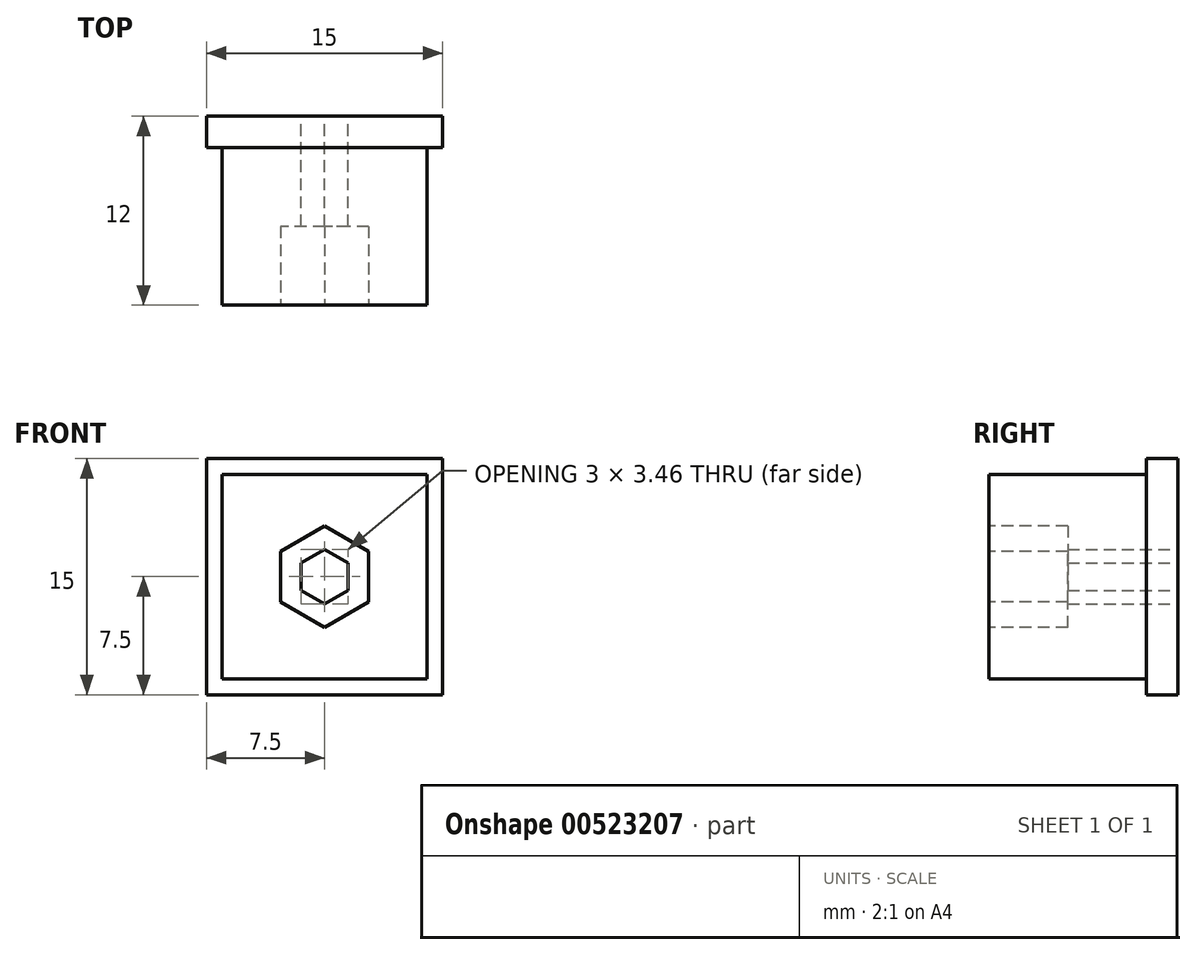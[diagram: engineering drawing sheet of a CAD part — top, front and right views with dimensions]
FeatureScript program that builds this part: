
annotation { "Feature Type Name" : "Feature", "Feature Type Description" : "" }
export const myFeature = defineFeature(function(context is Context, id is Id, definition is map)
    precondition{}
    {
        {
            var Q0;
            Q0=qCreatedBy(makeId("Front.planeOp"),FACE);
            var sketch = newSketch(context, id + "F0", { "sketchPlane" : qUnion([Q0])});
            skLineSegment(sketch, "E0.bottom", {"start": v(7.5, -7.5) * mm, "end": v(-7.5, -7.5) * mm});
            skLineSegment(sketch, "E0.top", {"start": v(7.5, 7.5) * mm, "end": v(-7.5, 7.5) * mm});
            skLineSegment(sketch, "E0.left", {"start": v(7.5, -7.5) * mm, "end": v(7.5, 7.5) * mm});
            skLineSegment(sketch, "E0.right", {"start": v(-7.5, -7.5) * mm, "end": v(-7.5, 7.5) * mm});
            skPoint(sketch, "E0.middle", {"position": v(0, 0) * mm});
            skSolve(sketch);
        }
        {
            var Q0;
            Q0=makeQuery(id+"F0.imprint","IMPRINT",FACE,{"disambiguationData":[TD([[makeQuery(id+"F0.imprint","IMPRINT",EDGE,{"derivedFrom":sQuery(id+"F0.wireOp",EDGE,"E0.bottom")}),-1.0]])]});
            extrude(context, id + "F1", {"entities" : qUnion([Q0]), "depth" : 2 * mm, "offsetDistance" : 25 * mm});
        }
        {
            var Q0;
            Q0=makeQuery(id+"F1.opExtrude","CAP_FACE",FACE,{"disambiguationData":[OSD([sQuery(id+"F0.wireOp",EDGE,"E0.bottom"),sQuery(id+"F0.wireOp",EDGE,"E0.top"),sQuery(id+"F0.wireOp",EDGE,"E0.left"),sQuery(id+"F0.wireOp",EDGE,"E0.right")])],"isStart":false});
            var sketch = newSketch(context, id + "F2", { "sketchPlane" : qUnion([Q0])});
            skLineSegment(sketch, "E1.0.0", {"start": v(7.5, -7.5) * mm, "end": v(7.5, 7.5) * mm});
            skLineSegment(sketch, "E1.0.1", {"start": v(7.5, 7.5) * mm, "end": v(-7.5, 7.5) * mm});
            skLineSegment(sketch, "E1.0.2", {"start": v(-7.5, 7.5) * mm, "end": v(-7.5, -7.5) * mm});
            skLineSegment(sketch, "E1.0.3", {"start": v(-7.5, -7.5) * mm, "end": v(7.5, -7.5) * mm});
            skLineSegment(sketch, "E2.0", {"start": v(6.5, -6.5) * mm, "end": v(6.5, 6.5) * mm});
            skLineSegment(sketch, "E2.1", {"start": v(-6.5, -6.5) * mm, "end": v(6.5, -6.5) * mm});
            skLineSegment(sketch, "E2.2", {"start": v(-6.5, 6.5) * mm, "end": v(-6.5, -6.5) * mm});
            skLineSegment(sketch, "E2.3", {"start": v(6.5, 6.5) * mm, "end": v(-6.5, 6.5) * mm});
            skSolve(sketch);
        }
        {
            var Q0;
            Q0=makeQuery(id+"F2.imprint","IMPRINT",FACE,{"disambiguationData":[TD([[makeQuery(id+"F2.imprint","IMPRINT",EDGE,{"derivedFrom":sQuery(id+"F2.wireOp",EDGE,"E2.0")}),1.0]])]});
            extrude(context, id + "F3", {"entities" : qUnion([Q0]), "operationType" : NewBodyOperationType.ADD, "depth" : 10 * mm, "offsetDistance" : 25 * mm});
        }
        {
            var Q0;
            Q0=makeQuery(id+"F1.opExtrude","CAP_FACE",FACE,{"disambiguationData":[OSD([sQuery(id+"F0.wireOp",EDGE,"E0.bottom"),sQuery(id+"F0.wireOp",EDGE,"E0.top"),sQuery(id+"F0.wireOp",EDGE,"E0.left"),sQuery(id+"F0.wireOp",EDGE,"E0.right")])],"isStart":true});
            var sketch = newSketch(context, id + "F4", { "sketchPlane" : qUnion([Q0])});
            skCircle(sketch, "E3.cCircle", {"center": v(0, 0) * mm, "radius": 1.5 * mm, "construction": true});
            skLineSegment(sketch, "E3.0", {"start": v(1.5, 0.87) * mm, "end": v(1.5, -0.87) * mm});
            skLineSegment(sketch, "E3.1", {"start": v(1.5, -0.87) * mm, "end": v(0, -1.73) * mm});
            skLineSegment(sketch, "E3.2", {"start": v(0, -1.73) * mm, "end": v(-1.5, -0.87) * mm});
            skLineSegment(sketch, "E3.3", {"start": v(-1.5, -0.87) * mm, "end": v(-1.5, 0.87) * mm});
            skLineSegment(sketch, "E3.4", {"start": v(-1.5, 0.87) * mm, "end": v(0, 1.73) * mm});
            skLineSegment(sketch, "E3.5", {"start": v(0, 1.73) * mm, "end": v(1.5, 0.87) * mm});
            skPoint(sketch, "E3.0.midPoint", {"position": v(1.5, 0) * mm});
            skSolve(sketch);
        }
        {
            var Q0;
            Q0=makeQuery(id+"F4.imprint","IMPRINT",FACE,{"disambiguationData":[TD([[makeQuery(id+"F4.imprint","IMPRINT",EDGE,{"derivedFrom":sQuery(id+"F4.wireOp",EDGE,"W7pu7vk7-25iV-fgy8-9aF9-MsBdlh5b4NGt")}),1.0]])]});
            var Q1;
            Q1=makeQuery(id+"F4.imprint","IMPRINT",FACE,{"disambiguationData":[TD([[makeQuery(id+"F4.imprint","IMPRINT",EDGE,{"derivedFrom":sQuery(id+"F4.wireOp",EDGE,"E3.0")}),-1.0]])]});
            extrude(context, id + "F5", {"entities" : qUnion([Q0, Q1]), "operationType" : NewBodyOperationType.REMOVE, "endBound" : BoundingType.UP_TO_NEXT, "oppositeDirection" : true, "depth" : 25 * mm, "offsetDistance" : 25 * mm});
        }
        {
            var Q0;
            Q0=makeQuery(id+"F3.opExtrude","CAP_FACE",FACE,{"disambiguationData":[OSD([sQuery(id+"F2.wireOp",EDGE,"E2.0"),sQuery(id+"F2.wireOp",EDGE,"E2.1"),sQuery(id+"F2.wireOp",EDGE,"E2.2"),sQuery(id+"F2.wireOp",EDGE,"E2.3")])],"isStart":false});
            var sketch = newSketch(context, id + "F6", { "sketchPlane" : qUnion([Q0])});
            skCircle(sketch, "E4.cCircle", {"center": v(0, 0) * mm, "radius": 2.8 * mm, "construction": true});
            skLineSegment(sketch, "E4.0", {"start": v(-2.8, -1.62) * mm, "end": v(-2.8, 1.62) * mm});
            skLineSegment(sketch, "E4.1", {"start": v(-2.8, 1.62) * mm, "end": v(0, 3.23) * mm});
            skLineSegment(sketch, "E4.2", {"start": v(0, 3.23) * mm, "end": v(2.8, 1.62) * mm});
            skLineSegment(sketch, "E4.3", {"start": v(2.8, 1.62) * mm, "end": v(2.8, -1.62) * mm});
            skLineSegment(sketch, "E4.4", {"start": v(2.8, -1.62) * mm, "end": v(0, -3.23) * mm});
            skLineSegment(sketch, "E4.5", {"start": v(0, -3.23) * mm, "end": v(-2.8, -1.62) * mm});
            skPoint(sketch, "E4.0.midPoint", {"position": v(-2.8, 0) * mm});
            skSolve(sketch);
        }
        {
            var Q0;
            Q0=makeQuery(id+"F6.imprint","IMPRINT",FACE,{"disambiguationData":[TD([[makeQuery(id+"F6.imprint","IMPRINT",EDGE,{"derivedFrom":sQuery(id+"F6.wireOp",EDGE,"E4.0")}),-1.0]])]});
            extrude(context, id + "F7", {"entities" : qUnion([Q0]), "operationType" : NewBodyOperationType.REMOVE, "oppositeDirection" : true, "depth" : 5 * mm, "offsetDistance" : 25 * mm});
        }
    });
